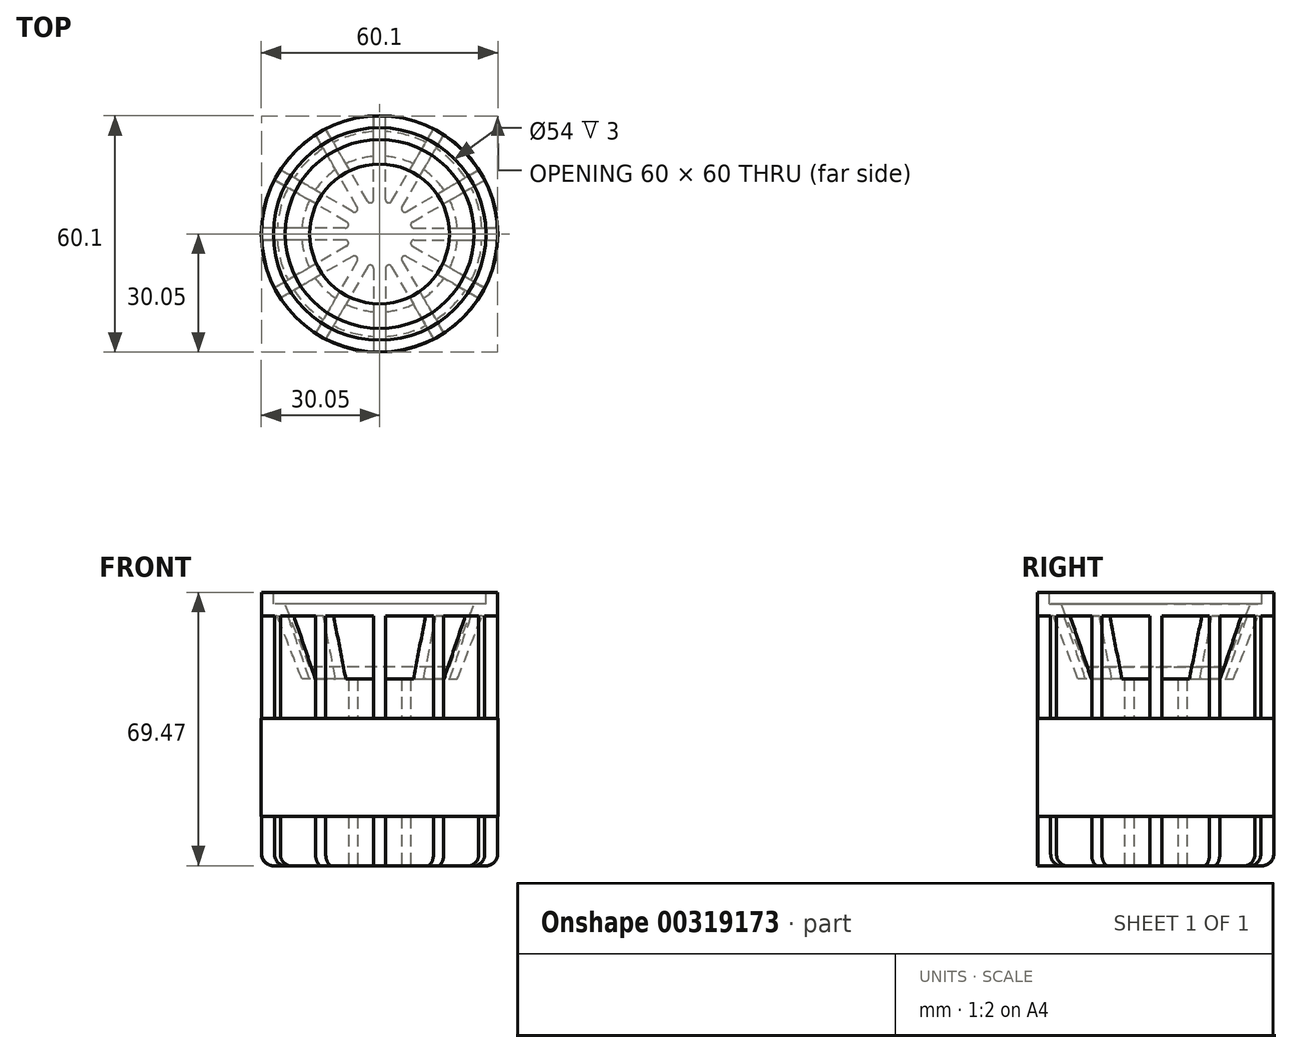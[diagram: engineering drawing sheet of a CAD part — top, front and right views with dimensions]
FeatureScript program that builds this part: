
annotation { "Feature Type Name" : "Feature", "Feature Type Description" : "" }
export const myFeature = defineFeature(function(context is Context, id is Id, definition is map)
    precondition{}
    {
        {
            var Q0;
            Q0=qCreatedBy(makeId("Right.planeOp"),FACE);
            var sketch = newSketch(context, id + "F0", { "sketchPlane" : qUnion([Q0])});
            skLineSegment(sketch, "E0", {"start": v(0, -12.53) * mm, "end": v(-19.8, -12.53) * mm});
            skLineSegment(sketch, "E1", {"start": v(-19.8, -12.53) * mm, "end": v(-26.05, 3.47) * mm});
            skLineSegment(sketch, "E2", {"start": v(-26.05, 3.47) * mm, "end": v(-30, 3.47) * mm});
            skLineSegment(sketch, "E3", {"start": v(-30, 3.47) * mm, "end": v(-30, 9.47) * mm});
            skLineSegment(sketch, "E4", {"start": v(-30, 9.47) * mm, "end": v(-27, 9.47) * mm});
            skLineSegment(sketch, "E5.0", {"start": v(-17.74, -9.53) * mm, "end": v(-24, 6.47) * mm});
            skLineSegment(sketch, "E6.0", {"start": v(0, -9.53) * mm, "end": v(-17.74, -9.53) * mm});
            skLineSegment(sketch, "E7", {"start": v(-24, 6.47) * mm, "end": v(-27, 6.47) * mm});
            skLineSegment(sketch, "E8", {"start": v(-27, 6.47) * mm, "end": v(-27, 9.47) * mm});
            skLineSegment(sketch, "E9", {"start": v(0, -9.53) * mm, "end": v(0, -12.53) * mm});
            skSolve(sketch);
        }
        {
            var Q0;
            Q0=qSketchRegion(id+"F0",true);
            var Q1;
            Q1=sQuery(id+"F0.wireOp",EDGE,"E9");
            revolve(context, id + "F1", {"entities" : qUnion([Q0]), "axis" : qUnion([Q1]), "revolveType" : RevolveType.FULL});
        }
        {
            var Q0;
            Q0=qCreatedBy(makeId("Top.planeOp"),FACE);
            cPlane(context, id + "F2", {"entities" : qUnion([Q0]), "cplaneType" : CPlaneType.OFFSET, "offset" : 60 * mm, "oppositeDirection" : true, "width" : 150 * mm, "height" : 150 * mm});
        }
        {
            var Q0;
            Q0=qCreatedBy(id+"F2.planeOp",FACE);
            var sketch = newSketch(context, id + "F3", { "sketchPlane" : qUnion([Q0])});
            skCircle(sketch, "E10", {"center": v(0, 0) * mm, "radius": 8.89 * mm, "construction": true});
            skPoint(sketch, "E11.center.orphan", {"position": v(0, -8.89) * mm});
            skPoint(sketch, "E12.center.orphan", {"position": v(0, 8.89) * mm});
            skArc(sketch, "E13", {"start": v(-3.08, -8.34) * mm, "mid": v(-2.13, -7.94) * mm, "end": v(-1.5, -8.76) * mm});
            skArc(sketch, "E14", {"start": v(-5.68, -6.84) * mm, "mid": v(-5.82, -5.82) * mm, "end": v(-6.84, -5.68) * mm});
            skArc(sketch, "E15", {"start": v(-8.76, -1.5) * mm, "mid": v(-7.94, -2.13) * mm, "end": v(-8.34, -3.08) * mm});
            skArc(sketch, "E16.MirrorCS", {"start": v(-8.76, 1.5) * mm, "mid": v(-7.94, 2.13) * mm, "end": v(-8.34, 3.08) * mm});
            skArc(sketch, "E17.MirrorCS", {"start": v(-5.68, 6.84) * mm, "mid": v(-5.82, 5.82) * mm, "end": v(-6.84, 5.68) * mm});
            skArc(sketch, "E18.MirrorCS", {"start": v(-3.08, 8.34) * mm, "mid": v(-2.13, 7.94) * mm, "end": v(-1.5, 8.76) * mm});
            skArc(sketch, "E19.MirrorCS", {"start": v(3.08, -8.34) * mm, "mid": v(2.13, -7.94) * mm, "end": v(1.5, -8.76) * mm});
            skArc(sketch, "E20.MirrorCS", {"start": v(5.68, -6.84) * mm, "mid": v(5.82, -5.82) * mm, "end": v(6.84, -5.68) * mm});
            skArc(sketch, "E21.MirrorCS", {"start": v(8.76, -1.5) * mm, "mid": v(7.94, -2.13) * mm, "end": v(8.34, -3.08) * mm});
            skArc(sketch, "E22.MirrorCS", {"start": v(8.76, 1.5) * mm, "mid": v(7.94, 2.13) * mm, "end": v(8.34, 3.08) * mm});
            skArc(sketch, "E23.MirrorCS", {"start": v(5.68, 6.84) * mm, "mid": v(5.82, 5.82) * mm, "end": v(6.84, 5.68) * mm});
            skArc(sketch, "E24.MirrorCS", {"start": v(3.08, 8.34) * mm, "mid": v(2.13, 7.94) * mm, "end": v(1.5, 8.76) * mm});
            skPoint(sketch, "E25.orphan", {"position": v(-8.76, 1.5) * mm});
            skPoint(sketch, "E26.orphan", {"position": v(-8.34, 3.08) * mm});
            skPoint(sketch, "E27.orphan", {"position": v(-6.84, 5.68) * mm});
            skPoint(sketch, "E28.orphan", {"position": v(-5.68, 6.84) * mm});
            skLineSegment(sketch, "E29", {"start": v(-1.5, -8.76) * mm, "end": v(-1.5, -29.96) * mm});
            skLineSegment(sketch, "E30", {"start": v(1.5, -8.76) * mm, "end": v(1.5, -29.96) * mm});
            skArc(sketch, "E31", {"start": v(-1.5, -29.96) * mm, "mid": v(0, -30) * mm, "end": v(1.5, -29.96) * mm});
            skArc(sketch, "E32.1.0", {"start": v(-16.28, -25.2) * mm, "mid": v(-15, -25.98) * mm, "end": v(-13.68, -26.7) * mm});
            skLineSegment(sketch, "E32.1.1", {"start": v(-5.68, -6.84) * mm, "end": v(-16.28, -25.2) * mm});
            skLineSegment(sketch, "E32.1.2", {"start": v(-3.08, -8.34) * mm, "end": v(-13.68, -26.7) * mm});
            skArc(sketch, "E32.2.0", {"start": v(-26.7, -13.68) * mm, "mid": v(-25.98, -15) * mm, "end": v(-25.2, -16.28) * mm});
            skLineSegment(sketch, "E32.2.1", {"start": v(-8.34, -3.08) * mm, "end": v(-26.7, -13.68) * mm});
            skLineSegment(sketch, "E32.2.2", {"start": v(-6.84, -5.68) * mm, "end": v(-25.2, -16.28) * mm});
            skArc(sketch, "E32.3.0", {"start": v(-29.96, 1.5) * mm, "mid": v(-30, 0) * mm, "end": v(-29.96, -1.5) * mm});
            skLineSegment(sketch, "E32.3.1", {"start": v(-8.76, 1.5) * mm, "end": v(-29.96, 1.5) * mm});
            skLineSegment(sketch, "E32.3.2", {"start": v(-8.76, -1.5) * mm, "end": v(-29.96, -1.5) * mm});
            skLineSegment(sketch, "E33", {"start": v(0, -33.33) * mm, "end": v(0, 31.28) * mm, "construction": true});
            skLineSegment(sketch, "E34", {"start": v(-35.42, 0) * mm, "end": v(33.93, 0) * mm, "construction": true});
            skLineSegment(sketch, "E35.MirrorCS", {"start": v(3.08, -8.34) * mm, "end": v(13.68, -26.7) * mm});
            skLineSegment(sketch, "E36.MirrorCS", {"start": v(5.68, -6.84) * mm, "end": v(16.28, -25.2) * mm});
            skLineSegment(sketch, "E37.MirrorCS", {"start": v(6.84, -5.68) * mm, "end": v(25.2, -16.28) * mm});
            skLineSegment(sketch, "E38.MirrorCS", {"start": v(8.34, -3.08) * mm, "end": v(26.7, -13.68) * mm});
            skLineSegment(sketch, "E39.MirrorCS", {"start": v(8.76, -1.5) * mm, "end": v(29.96, -1.5) * mm});
            skLineSegment(sketch, "E40.MirrorCS", {"start": v(8.76, 1.5) * mm, "end": v(29.96, 1.5) * mm});
            skArc(sketch, "E41.MirrorCS", {"start": v(29.96, 1.5) * mm, "mid": v(30, 0) * mm, "end": v(29.96, -1.5) * mm});
            skArc(sketch, "E42.MirrorCS", {"start": v(26.7, -13.68) * mm, "mid": v(25.98, -15) * mm, "end": v(25.2, -16.28) * mm});
            skArc(sketch, "E43.MirrorCS", {"start": v(16.28, -25.2) * mm, "mid": v(15, -25.98) * mm, "end": v(13.68, -26.7) * mm});
            skArc(sketch, "E44.MirrorCS", {"start": v(1.5, -29.96) * mm, "mid": v(0, -30) * mm, "end": v(-1.5, -29.96) * mm});
            skLineSegment(sketch, "E45.MirrorCS", {"start": v(-8.34, 3.08) * mm, "end": v(-26.7, 13.68) * mm});
            skLineSegment(sketch, "E46.MirrorCS", {"start": v(-6.84, 5.68) * mm, "end": v(-25.2, 16.28) * mm});
            skArc(sketch, "E47.MirrorCS", {"start": v(-26.7, 13.68) * mm, "mid": v(-25.98, 15) * mm, "end": v(-25.2, 16.28) * mm});
            skLineSegment(sketch, "E48.MirrorCS", {"start": v(-5.68, 6.84) * mm, "end": v(-16.28, 25.2) * mm});
            skArc(sketch, "E49.MirrorCS", {"start": v(-16.28, 25.2) * mm, "mid": v(-15, 25.98) * mm, "end": v(-13.68, 26.7) * mm});
            skLineSegment(sketch, "E50.MirrorCS", {"start": v(-3.08, 8.34) * mm, "end": v(-13.68, 26.7) * mm});
            skLineSegment(sketch, "E51.MirrorCS", {"start": v(-1.5, 8.76) * mm, "end": v(-1.5, 29.96) * mm});
            skLineSegment(sketch, "E52.MirrorCS", {"start": v(1.5, 8.76) * mm, "end": v(1.5, 29.96) * mm});
            skArc(sketch, "E53.MirrorCS", {"start": v(1.5, 29.96) * mm, "mid": v(0, 30) * mm, "end": v(-1.5, 29.96) * mm});
            skLineSegment(sketch, "E54.MirrorCS", {"start": v(3.08, 8.34) * mm, "end": v(13.68, 26.7) * mm});
            skLineSegment(sketch, "E55.MirrorCS", {"start": v(5.68, 6.84) * mm, "end": v(16.28, 25.2) * mm});
            skArc(sketch, "E56.MirrorCS", {"start": v(16.28, 25.2) * mm, "mid": v(15, 25.98) * mm, "end": v(13.68, 26.7) * mm});
            skLineSegment(sketch, "E57.MirrorCS", {"start": v(6.84, 5.68) * mm, "end": v(25.2, 16.28) * mm});
            skArc(sketch, "E58.MirrorCS", {"start": v(26.7, 13.68) * mm, "mid": v(25.98, 15) * mm, "end": v(25.2, 16.28) * mm});
            skLineSegment(sketch, "E59.MirrorCS", {"start": v(8.34, 3.08) * mm, "end": v(26.7, 13.68) * mm});
            skSolve(sketch);
        }
        {
            var Q0;
            Q0=qSketchRegion(id+"F3",true);
            var Q1;
            Q1=makeQuery(id+"F1.opRevolve","SWEPT_BODY",BODY,{"disambiguationData":[OSD([sQuery(id+"F0.wireOp",EDGE,"E0"),sQuery(id+"F0.wireOp",EDGE,"E1"),sQuery(id+"F0.wireOp",EDGE,"E2"),sQuery(id+"F0.wireOp",EDGE,"E3"),sQuery(id+"F0.wireOp",EDGE,"E4"),sQuery(id+"F0.wireOp",EDGE,"E5.0"),sQuery(id+"F0.wireOp",EDGE,"E6.0"),sQuery(id+"F0.wireOp",EDGE,"E7"),sQuery(id+"F0.wireOp",EDGE,"E8"),sQuery(id+"F0.wireOp",EDGE,"E9")])]});
            extrude(context, id + "F4", {"entities" : qUnion([Q0]), "operationType" : NewBodyOperationType.ADD, "endBound" : BoundingType.UP_TO_BODY, "endBoundEntityBody" : qUnion([Q1]), "depth" : 25 * mm});
        }
        {
            var Q0;
            Q0=makeQuery(id+"F4.opExtrude","CAP_EDGE",EDGE,{"disambiguationData":[OSD([sQuery(id+"F3.wireOp",EDGE,"E32.1.0")])],"isStart":true});
            var Q1;
            Q1=makeQuery(id+"F4.opExtrude","CAP_EDGE",EDGE,{"disambiguationData":[OSD([sQuery(id+"F3.wireOp",EDGE,"E32.2.0")])],"isStart":true});
            var Q2;
            Q2=makeQuery(id+"F4.opExtrude","CAP_EDGE",EDGE,{"disambiguationData":[OSD([sQuery(id+"F3.wireOp",EDGE,"E32.3.0")])],"isStart":true});
            var Q3;
            Q3=makeQuery(id+"F4.opExtrude","CAP_EDGE",EDGE,{"disambiguationData":[OSD([sQuery(id+"F3.wireOp",EDGE,"E47.MirrorCS")])],"isStart":true});
            var Q4;
            Q4=makeQuery(id+"F4.opExtrude","CAP_EDGE",EDGE,{"disambiguationData":[OSD([sQuery(id+"F3.wireOp",EDGE,"E49.MirrorCS")])],"isStart":true});
            var Q5;
            Q5=makeQuery(id+"F4.opExtrude","CAP_EDGE",EDGE,{"disambiguationData":[OSD([sQuery(id+"F3.wireOp",EDGE,"E53.MirrorCS")])],"isStart":true});
            var Q6;
            Q6=makeQuery(id+"F4.opExtrude","CAP_EDGE",EDGE,{"disambiguationData":[OSD([sQuery(id+"F3.wireOp",EDGE,"E56.MirrorCS")])],"isStart":true});
            var Q7;
            Q7=makeQuery(id+"F4.opExtrude","CAP_EDGE",EDGE,{"disambiguationData":[OSD([sQuery(id+"F3.wireOp",EDGE,"E58.MirrorCS")])],"isStart":true});
            var Q8;
            Q8=makeQuery(id+"F4.opExtrude","CAP_EDGE",EDGE,{"disambiguationData":[OSD([sQuery(id+"F3.wireOp",EDGE,"E41.MirrorCS")])],"isStart":true});
            var Q9;
            Q9=makeQuery(id+"F4.opExtrude","CAP_EDGE",EDGE,{"disambiguationData":[OSD([sQuery(id+"F3.wireOp",EDGE,"E42.MirrorCS")])],"isStart":true});
            var Q10;
            Q10=makeQuery(id+"F4.opExtrude","CAP_EDGE",EDGE,{"disambiguationData":[OSD([sQuery(id+"F3.wireOp",EDGE,"E43.MirrorCS")])],"isStart":true});
            var Q11;
            Q11=makeQuery(id+"F4.opExtrude","CAP_EDGE",EDGE,{"disambiguationData":[OSD([sQuery(id+"F3.wireOp",EDGE,"E44.MirrorCS")])],"isStart":true});
            fillet(context, id + "F5", {"entities" : qUnion([Q0, Q1, Q2, Q3, Q4, Q5, Q6, Q7, Q8, Q9, Q10, Q11]), "radius" : 3 * mm, "tangentPropagation" : true, "allowEdgeOverflow" : false});
        }
        {
            var Q0;
            Q0=qCreatedBy(id+"F2.planeOp",FACE);
            cPlane(context, id + "F6", {"entities" : qUnion([Q0]), "cplaneType" : CPlaneType.OFFSET, "offset" : 25 * mm, "width" : 150 * mm, "height" : 150 * mm});
        }
        {
            var Q0;
            Q0=qCreatedBy(id+"F6.planeOp",FACE);
            var sketch = newSketch(context, id + "F7", { "sketchPlane" : qUnion([Q0])});
            skCircle(sketch, "E60", {"center": v(0, 0) * mm, "radius": 30.05 * mm});
            skSolve(sketch);
        }
        {
            var Q0;
            Q0 = qSketchRegion(id + "F7", true);
            extrude(context, id + "F8", {"entities" : qUnion([Q0]), "operationType" : NewBodyOperationType.ADD, "endBound" : BoundingType.SYMMETRIC, "depth" : 25 * mm});
        }
    });
